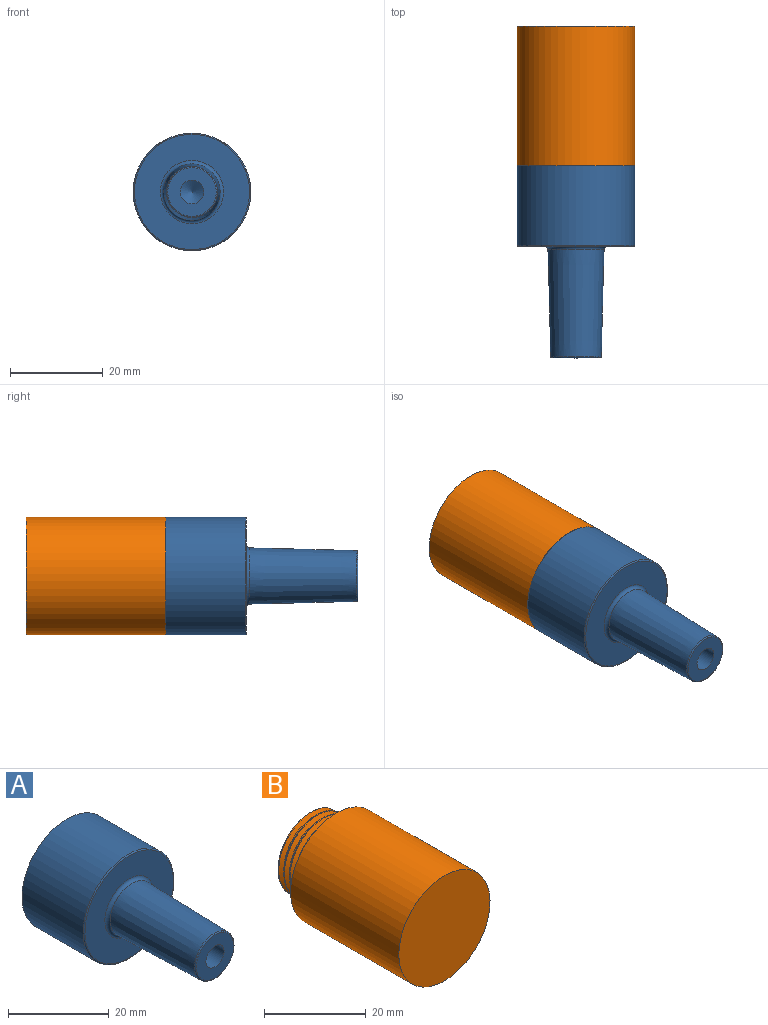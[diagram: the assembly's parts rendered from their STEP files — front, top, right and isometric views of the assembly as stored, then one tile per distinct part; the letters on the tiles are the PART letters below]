
ASSEMBLY  parts=2 mates=1
PART A: 18 faces, bbox 27.9x42.6x27.9 mm
  f0: cylinder r=8.64mm len=17.27mm, axis (0,1,0), area 136mm2, adj f11,f14,f15,f17
  f1: cylinder r=12.7mm len=25.4mm, axis (0,-1,0), area 1373.2mm2, adj f8,f10
  f2: plane 24.89x24.89mm, normal (0,-1,0), area 339.7mm2, adj f7,f8
  f3: cone r=6.1mm half-angle=1.4deg, axis (0,1,0), area 841.9mm2, adj f7,f9
  f4: plane 10.49x10.49mm, normal (0,-1,0), area 66mm2, adj f6,f9
  f5: cone r=0mm half-angle=59deg, axis (0,-1,0), area 23.9mm2, adj f6
  f6: cylinder r=2.55mm len=22.23mm, axis (0,-1,0), area 356.5mm2, adj f4,f5
  f7: torus R=6.84mm, axis (0,1,0), area 47.1mm2, adj f2,f3
  f8: torus R=12.45mm, axis (0,1,0), area 31.6mm2, adj f1,f2
  f9: torus R=5.25mm, axis (0,1,0), area 13.3mm2, adj f3,f4
  f10: plane 25.4x25.4mm, normal (0,1,0), area 190.5mm2, adj f1,f14
  f11: plane 20.25x20.25mm, normal (0,-1,0), area 58.1mm2, adj f0,f12,f15,f16,f17
  f12: cylinder r=9.91mm len=19.81mm, axis (0,1,0), area 296.4mm2, adj f11,f13
  f13: plane 19.81x19.81mm, normal (0,1,0), area 308.3mm2, adj f12
  f14: cone r=8.64mm half-angle=60deg, axis (0,1,0), area 76.4mm2, adj f0,f10,f15,f16,f17
  f15: bspline ~21.74x18.83mm, area 236.6mm2, adj f0,f11,f14,f16
  f16: cylinder r=9.42mm len=18.83mm, axis (0,1,0), area 36.2mm2, adj f11,f14,f15,f17
  f17: bspline ~21.74x18.83mm, area 236.5mm2, adj f0,f11,f14,f16
PART B: 11 faces, bbox 26x39.2x26 mm
  f0: plane 18.35x18.27mm, normal (0,-1,0), area 39.2mm2, adj f2,f3,f8,f9,f10
  f1: plane 25.4x25.4mm, normal (0,1,0), area 299.2mm2, adj f2,f5
  f2: cylinder r=8.13mm len=16.26mm, axis (0,1,0), area 121.6mm2, adj f0,f1
  f3: cylinder r=9.35mm len=18.71mm, axis (0,1,0), area 34.5mm2, adj f0,f7,f8,f9
  f4: plane 15.91x15.91mm, normal (0,1,0), area 198.9mm2, adj f7
  f5: cylinder r=12.7mm len=30.16mm, axis (0,-1,0), area 2406.9mm2, adj f1,f6
  f6: plane 25.4x25.4mm, normal (0,-1,0), area 506.7mm2, adj f5
  f7: cone r=7.96mm half-angle=60deg, axis (0,-1,0), area 55.4mm2, adj f3,f4,f8,f9,f10
  f8: bspline ~22x19.05mm, area 187mm2, adj f0,f3,f7,f10
  f9: bspline ~22x19.05mm, area 186.9mm2, adj f0,f3,f7,f10
  f10: cylinder r=8.44mm len=16.87mm, axis (0,1,0), area 57.4mm2, adj f0,f7,f8,f9
PLACE A at identity fixed
PLACE B rot(axis=(0,0,1),180deg) t=(0,22.22,0)mm
MATE revolute A.f0 <-> B.f2  axis (0,1,0) through (0,17.46,0)mm
